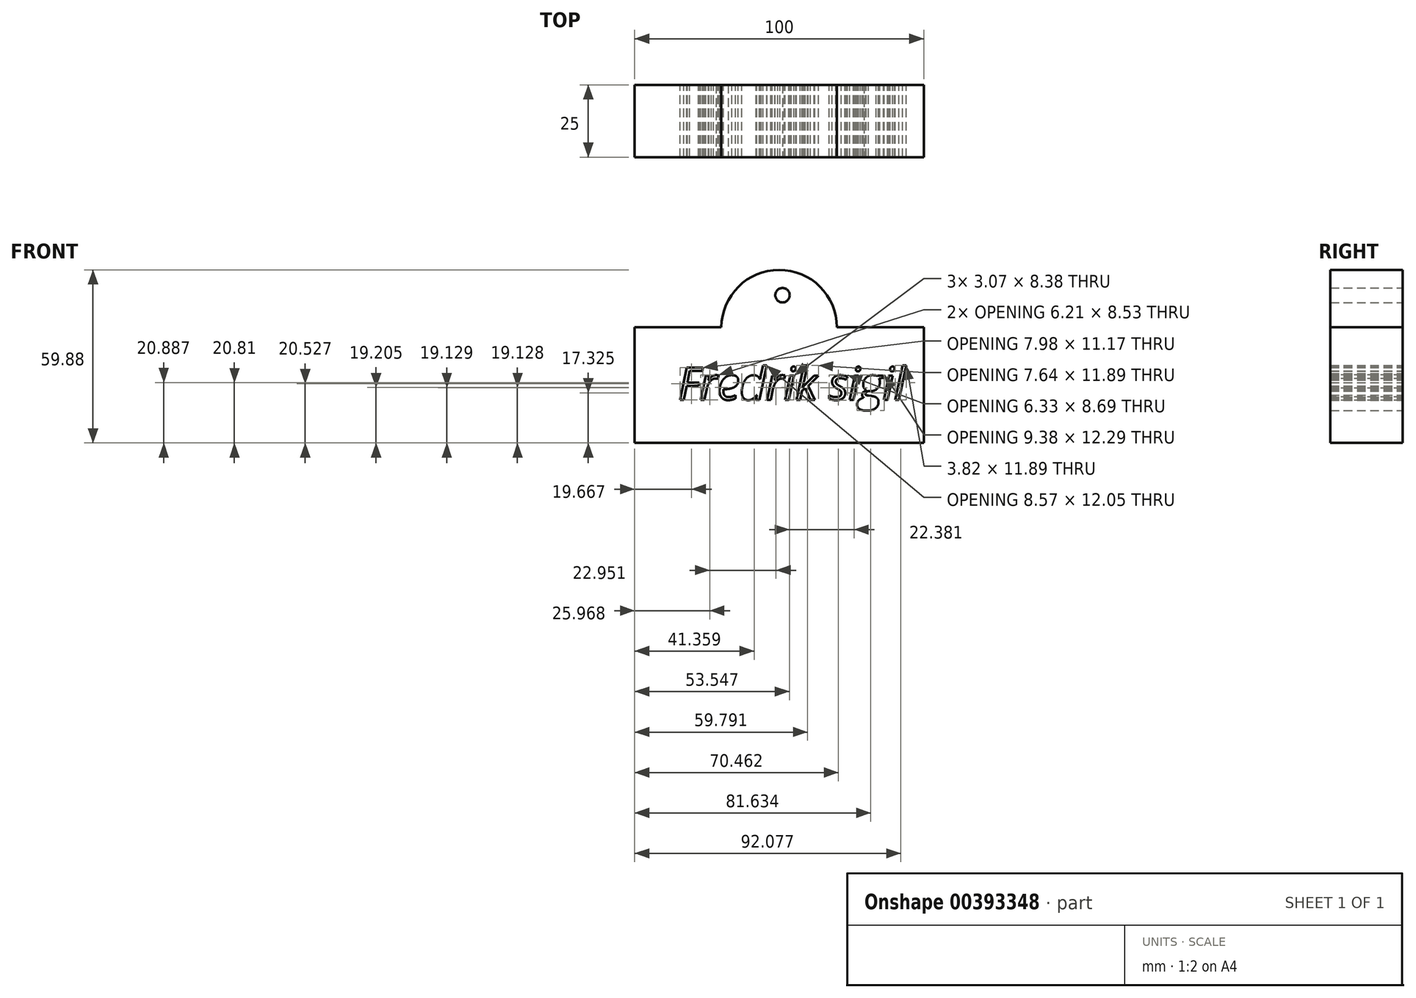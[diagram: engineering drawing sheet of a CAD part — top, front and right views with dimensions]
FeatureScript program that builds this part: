
annotation { "Feature Type Name" : "Feature", "Feature Type Description" : "" }
export const myFeature = defineFeature(function(context is Context, id is Id, definition is map)
    precondition{}
    {
        {
            var Q0;
            Q0=qCreatedBy(makeId("Front.planeOp"),FACE);
            var sketch = newSketch(context, id + "F0", { "sketchPlane" : qUnion([Q0])});
            skLineSegment(sketch, "E0.top", {"start": v(-51.15, 12.76) * mm, "end": v(48.85, 12.76) * mm});
            skLineSegment(sketch, "E0.left", {"start": v(-51.15, 52.76) * mm, "end": v(-51.15, 12.76) * mm});
            skLineSegment(sketch, "E0.right", {"start": v(48.85, 52.76) * mm, "end": v(48.85, 12.76) * mm});
            skPoint(sketch, "E1", {"position": v(-1.15, 52.76) * mm});
            skPoint(sketch, "E2", {"position": v(-21.15, 52.76) * mm});
            skPoint(sketch, "E3", {"position": v(18.85, 52.76) * mm});
            skArc(sketch, "E4", {"start": v(18.85, 52.76) * mm, "mid": v(-1.15, 72.64) * mm, "end": v(-21.15, 52.76) * mm});
            skLineSegment(sketch, "E5", {"start": v(-51.15, 52.76) * mm, "end": v(-21.15, 52.76) * mm});
            skLineSegment(sketch, "E6", {"start": v(18.85, 52.76) * mm, "end": v(48.85, 52.76) * mm});
            skCircle(sketch, "E7", {"center": v(0, 63.87) * mm, "radius": 2.5 * mm});
            skText(sketch, "E8", { "text": "Fredrik sigil", "fontName": "OpenSans-Italic.ttf"});
            const initialGuessF0  = {"E8": [-0.03613, 0.0277, 1, 0, 0.01127]};
            skSetInitialGuess(sketch, initialGuessF0);
            skSolve(sketch);
        }
        {
            var Q0;
            Q0=makeQuery(id+"F0.imprint","IMPRINT",FACE,{"disambiguationData":[TD([[makeQuery(id+"F0.imprint","IMPRINT",EDGE,{"derivedFrom":sQuery(id+"F0.wireOp",EDGE,"E0.top")}),1.0]])]});
            extrude(context, id + "F1", {"entities" : qUnion([Q0]), "depth" : 25 * mm});
        }
    });
